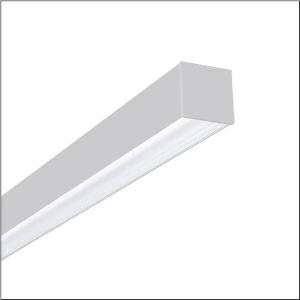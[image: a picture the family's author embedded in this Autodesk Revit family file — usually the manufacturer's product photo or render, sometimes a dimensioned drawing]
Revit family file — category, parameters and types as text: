
# Revit family: silica_r_5mx21bd2w4a_b787
name_source: partatom
category: Lighting Fixtures
units: mm (PartAtom-declared; Revit-internal decimal feet)

## family parameters
Cut with Voids When Loaded = No
Host = Face
Light Source = No
Part Type = Normal
Room Calculation Point = No
Round Connector Dimension = Use Diameter
Shared = No

## types (1)
- --- (1 x LED, 9910 lm, 60.1 W, 4000K)
    Apparent Load = 60 VA
    CIE Flux Codes = 82 97 100 100 100
    Color Rendering = 80
    Color Temperature = 4000K
    Default Elevation = 1800 mm
    Description = Silica®, office luminaire, of aluminium, light emission: direct distribution, primary light characteristic: symmetric, installation type: surface-mounted, LED, rated luminous flux: 9.910lm, luminous efficacy: 165lm/W, light colour: 840, colour temperature: 4000K, control gear: ECG DALI, with terminal, 3+2-pole, max. 2.5mm², mains connection: 230V, AC, 50/60Hz, rated input power: 60W, luminaire housing, of aluminium, traffic white (RAL 9016), length: 2.844mm, width: 65mm, height: 64mm, protection rating (complete): IP20, insulation class (complete): insulation class I (protective earthing), certification: CE, permissible operating ambient temperature: 0..+35°C, standard: EN 50419, packaging unit: 1 piece
    Height = 64 mm
    Lamp = 1 x LED
    Lamp Light Flux = 9910 lm
    Lamp Power = 60.1 W
    Lamp count = 1
    Length = 2845 mm
    Luminous efficacy = 165 lm/W
    Manufacturer = Siteco
    ModVariant = No
    Model = 5MX21BD2W4A
    Mounting Place = Ceiling
    Mounting Type = Surface mounted
    Number of Poles = 1
    OnlyDefault = Yes
    Power Factor = 1
    Product Name = Silica®
    Product group = office luminaire | ceiling mounted
    ProductGroupID = 300
    Protection Class = Protection class I
    Protection Degree = IP 20
    RLX_Detail_Level = 1
    RLX_Emergency_Light_Flux = 0 lm
    RLX_Emergency_Type = 0
    RLX_Emergency_Type_DB = No
    RlxData = <blob elided: 23297 chars, md5=c74cc3be>
    Socket = socket
    Standby Power = 0 W
    System Light Flux = 9910 lm
    System Power = 60 W
    Type Comments = factory setting: luminous flux: 100 % | dim-lin: 254 | 336 mA
    Type Image = l_1003937.jpg
    URL = http://relux.com
    VarID = @adj_155508
    Voltage = 0 V
    Weight = 0.00 kg
    Width = 66 mm

## geometry (parser evidence)
native form markers: Blend x4, Sweep x11
no freeform markers — native parametric forms only
